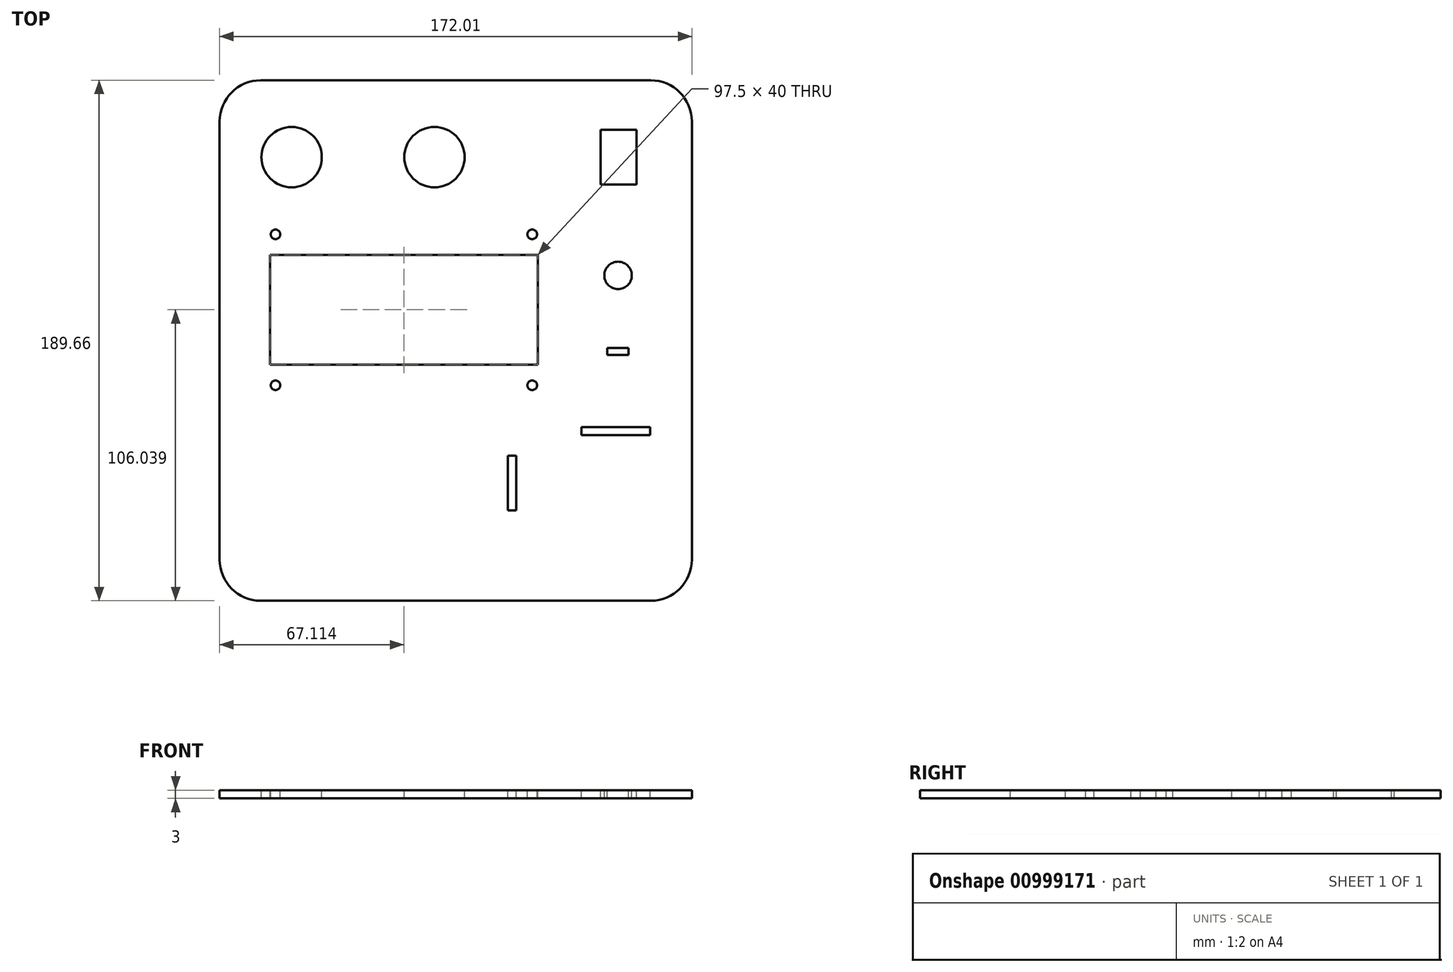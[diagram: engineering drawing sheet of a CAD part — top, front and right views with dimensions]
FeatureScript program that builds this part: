
annotation { "Feature Type Name" : "Feature", "Feature Type Description" : "" }
export const myFeature = defineFeature(function(context is Context, id is Id, definition is map)
    precondition{}
    {
        {
            var Q0;
            Q0=qCreatedBy(makeId("Top.planeOp"),FACE);
            var sketch = newSketch(context, id + "F0", { "sketchPlane" : qUnion([Q0])});
            skPoint(sketch, "E0.middle", {"position": v(0, 0) * mm});
            skLineSegment(sketch, "E1.bottom", {"start": v(124.5, -135.5) * mm, "end": v(-124.5, -135.5) * mm});
            skLineSegment(sketch, "E1.top", {"start": v(124.5, 135.5) * mm, "end": v(-124.5, 135.5) * mm});
            skLineSegment(sketch, "E1.left", {"start": v(124.5, -135.5) * mm, "end": v(124.5, 135.5) * mm});
            skLineSegment(sketch, "E1.right", {"start": v(-124.5, -135.5) * mm, "end": v(-124.5, 135.5) * mm});
            skLineSegment(sketch, "E2.0", {"start": v(113.5, 124.5) * mm, "end": v(-113.5, 124.5) * mm});
            skLineSegment(sketch, "E2.1", {"start": v(113.5, -124.5) * mm, "end": v(113.5, 124.5) * mm});
            skLineSegment(sketch, "E2.2", {"start": v(113.5, -124.5) * mm, "end": v(-113.5, -124.5) * mm});
            skLineSegment(sketch, "E2.3", {"start": v(-113.5, -124.5) * mm, "end": v(-113.5, 124.5) * mm});
            skSolve(sketch);
        }
        {
            var Q0;
            Q0 = qSketchRegion(id + "F0", true);
            var Q1;
            Q1=makeQuery(id+"F0.imprint","IMPRINT",FACE,{"disambiguationData":[TD([[makeQuery(id+"F0.imprint","IMPRINT",EDGE,{"derivedFrom":sQuery(id+"F0.wireOp",EDGE,"E2.0")}),1.0]])]});
            extrude(context, id + "F1", {"entities" : qUnion([Q0, Q1]), "depth" : 3 * mm, "offsetDistance" : 25 * mm});
        }
        {
            var Q0;
            Q0=makeQuery(id+"F1.opExtrude","CAP_FACE",FACE,{"disambiguationData":[OSD([sQuery(id+"F0.wireOp",EDGE,"E1.bottom"),sQuery(id+"F0.wireOp",EDGE,"E1.top"),sQuery(id+"F0.wireOp",EDGE,"E1.left"),sQuery(id+"F0.wireOp",EDGE,"E1.right")])],"isStart":false});
            var sketch = newSketch(context, id + "F2", { "sketchPlane" : qUnion([Q0])});
            skLineSegment(sketch, "E3.bottom", {"start": v(54.76, 20.35) * mm, "end": v(-42.74, 20.35) * mm});
            skLineSegment(sketch, "E3.top", {"start": v(54.76, 60.35) * mm, "end": v(-42.74, 60.35) * mm});
            skLineSegment(sketch, "E3.left", {"start": v(54.76, 20.35) * mm, "end": v(54.76, 60.35) * mm});
            skLineSegment(sketch, "E3.right", {"start": v(-42.74, 20.35) * mm, "end": v(-42.74, 60.35) * mm});
            skPoint(sketch, "E3.middle", {"position": v(6.01, 40.35) * mm});
            skLineSegment(sketch, "E4.bottom", {"start": v(44.01, -42.25) * mm, "end": v(-31.99, -42.25) * mm, "construction": true});
            skLineSegment(sketch, "E4.top", {"start": v(44.01, -3.25) * mm, "end": v(-31.99, -3.25) * mm, "construction": true});
            skLineSegment(sketch, "E4.left", {"start": v(54.01, -32.25) * mm, "end": v(54.01, -13.25) * mm, "construction": true});
            skLineSegment(sketch, "E4.right", {"start": v(-41.99, -32.25) * mm, "end": v(-41.99, -13.25) * mm, "construction": true});
            skPoint(sketch, "E4.middle", {"position": v(6.01, -22.75) * mm});
            skPoint(sketch, "E5.visualSharp", {"position": v(-41.99, -3.25) * mm});
            skArc(sketch, "E5.filletArc", {"start": v(-31.99, -3.25) * mm, "mid": v(-39.06, -6.18) * mm, "end": v(-41.99, -13.25) * mm, "construction": true});
            skPoint(sketch, "E6.visualSharp", {"position": v(-41.99, -42.25) * mm});
            skArc(sketch, "E6.filletArc", {"start": v(-41.99, -32.25) * mm, "mid": v(-39.06, -39.32) * mm, "end": v(-31.99, -42.25) * mm, "construction": true});
            skPoint(sketch, "E7.visualSharp", {"position": v(54.01, -42.25) * mm});
            skArc(sketch, "E7.filletArc", {"start": v(44.01, -42.25) * mm, "mid": v(51.09, -39.32) * mm, "end": v(54.01, -32.25) * mm, "construction": true});
            skPoint(sketch, "E8.visualSharp", {"position": v(54.01, -3.25) * mm});
            skArc(sketch, "E8.filletArc", {"start": v(54.01, -13.25) * mm, "mid": v(51.09, -6.18) * mm, "end": v(44.01, -3.25) * mm, "construction": true});
            skCircle(sketch, "E9", {"center": v(-34.87, 95.98) * mm, "radius": 11 * mm});
            skCircle(sketch, "E10", {"center": v(17.17, 95.98) * mm, "radius": 11 * mm});
            skLineSegment(sketch, "E11.bottom", {"start": v(52.76, 12.85) * mm, "end": v(-40.74, 12.85) * mm, "construction": true});
            skLineSegment(sketch, "E11.top", {"start": v(52.76, 67.85) * mm, "end": v(-40.74, 67.85) * mm, "construction": true});
            skLineSegment(sketch, "E11.left", {"start": v(52.76, 12.85) * mm, "end": v(52.76, 67.85) * mm, "construction": true});
            skLineSegment(sketch, "E11.right", {"start": v(-40.74, 12.85) * mm, "end": v(-40.74, 67.85) * mm, "construction": true});
            skCircle(sketch, "E12", {"center": v(-40.74, 67.85) * mm, "radius": 1.75 * mm});
            skCircle(sketch, "E13", {"center": v(52.76, 67.85) * mm, "radius": 1.75 * mm});
            skCircle(sketch, "E14", {"center": v(52.76, 12.85) * mm, "radius": 1.75 * mm});
            skCircle(sketch, "E15", {"center": v(-40.74, 12.85) * mm, "radius": 1.75 * mm});
            skLineSegment(sketch, "E16", {"start": v(6.01, 40.35) * mm, "end": v(6.01, -22.75) * mm, "construction": true});
            skLineSegment(sketch, "E17.bottom", {"start": v(43.95, -32.75) * mm, "end": v(46.95, -32.75) * mm});
            skLineSegment(sketch, "E17.top", {"start": v(43.95, -12.75) * mm, "end": v(46.95, -12.75) * mm});
            skLineSegment(sketch, "E17.left", {"start": v(43.95, -32.75) * mm, "end": v(43.95, -12.75) * mm});
            skLineSegment(sketch, "E17.right", {"start": v(46.95, -32.75) * mm, "end": v(46.95, -12.75) * mm});
            skPoint(sketch, "E17.middle", {"position": v(45.45, -22.75) * mm});
            skPoint(sketch, "E17.middle.positionSnap0", {"position": v(54.01, -22.75) * mm});
            skPoint(sketch, "E17.centerSnap0", {"position": v(54.01, -22.75) * mm});
            skLineSegment(sketch, "E18.bottom", {"start": v(90.7, 85.98) * mm, "end": v(77.7, 85.98) * mm});
            skLineSegment(sketch, "E18.top", {"start": v(90.7, 105.98) * mm, "end": v(77.7, 105.98) * mm});
            skLineSegment(sketch, "E18.left", {"start": v(90.7, 85.98) * mm, "end": v(90.7, 105.98) * mm});
            skLineSegment(sketch, "E18.right", {"start": v(77.7, 85.98) * mm, "end": v(77.7, 105.98) * mm});
            skPoint(sketch, "E18.middle", {"position": v(84.2, 95.98) * mm});
            skLineSegment(sketch, "E19.bottom", {"start": v(70.65, -2.33) * mm, "end": v(95.65, -2.33) * mm});
            skLineSegment(sketch, "E19.top", {"start": v(70.65, -5.33) * mm, "end": v(95.65, -5.33) * mm});
            skLineSegment(sketch, "E19.left", {"start": v(70.65, -2.33) * mm, "end": v(70.65, -5.33) * mm});
            skLineSegment(sketch, "E19.right", {"start": v(95.65, -2.33) * mm, "end": v(95.65, -5.33) * mm});
            skLineSegment(sketch, "E20.bottom", {"start": v(65.56, -5.33) * mm, "end": v(100.56, -5.33) * mm, "construction": true});
            skLineSegment(sketch, "E20.top", {"start": v(65.56, -56.33) * mm, "end": v(100.56, -56.33) * mm, "construction": true});
            skLineSegment(sketch, "E20.left", {"start": v(65.56, -5.33) * mm, "end": v(65.56, -56.33) * mm, "construction": true});
            skLineSegment(sketch, "E20.right", {"start": v(100.56, -5.33) * mm, "end": v(100.56, -56.33) * mm, "construction": true});
            skCircle(sketch, "E21", {"center": v(84.01, 52.88) * mm, "radius": 5 * mm});
            skLineSegment(sketch, "E22.bottom", {"start": v(80.15, 26.44) * mm, "end": v(87.85, 26.44) * mm});
            skLineSegment(sketch, "E22.top", {"start": v(80.15, 23.94) * mm, "end": v(87.85, 23.94) * mm});
            skLineSegment(sketch, "E22.left", {"start": v(80.15, 26.44) * mm, "end": v(80.15, 23.94) * mm});
            skLineSegment(sketch, "E22.right", {"start": v(87.85, 26.44) * mm, "end": v(87.85, 23.94) * mm});
            skSolve(sketch);
        }
        {
            var Q0;
            Q0 = qSketchRegion(id + "F2", true);
            extrude(context, id + "F3", {"entities" : qUnion([Q0]), "operationType" : NewBodyOperationType.REMOVE, "oppositeDirection" : true, "depth" : 25 * mm, "offsetDistance" : 25 * mm});
        }
        {
            var Q0;
            Q0=makeQuery(id+"F1.opExtrude","CAP_FACE",FACE,{"disambiguationData":[OSD([sQuery(id+"F0.wireOp",EDGE,"E1.bottom"),sQuery(id+"F0.wireOp",EDGE,"E1.top"),sQuery(id+"F0.wireOp",EDGE,"E1.left"),sQuery(id+"F0.wireOp",EDGE,"E1.right")])],"isStart":false});
            var sketch = newSketch(context, id + "F4", { "sketchPlane" : qUnion([Q0])});
            skLineSegment(sketch, "E23.bottom", {"start": v(-46.1, 123.97) * mm, "end": v(95.9, 123.97) * mm});
            skLineSegment(sketch, "E23.top", {"start": v(-46.1, -65.69) * mm, "end": v(95.9, -65.69) * mm});
            skLineSegment(sketch, "E23.left", {"start": v(-61.1, 108.97) * mm, "end": v(-61.1, -50.69) * mm});
            skLineSegment(sketch, "E23.right", {"start": v(110.9, 108.97) * mm, "end": v(110.9, -50.69) * mm});
            skPoint(sketch, "E24.visualSharp", {"position": v(-61.1, 123.97) * mm});
            skArc(sketch, "E24.filletArc", {"start": v(-46.1, 123.97) * mm, "mid": v(-56.7, 119.58) * mm, "end": v(-61.1, 108.97) * mm});
            skPoint(sketch, "E25.visualSharp", {"position": v(-61.1, -65.69) * mm});
            skArc(sketch, "E25.filletArc", {"start": v(-61.1, -50.69) * mm, "mid": v(-56.7, -61.3) * mm, "end": v(-46.1, -65.69) * mm});
            skPoint(sketch, "E26.visualSharp", {"position": v(110.9, -65.69) * mm});
            skArc(sketch, "E26.filletArc", {"start": v(95.9, -65.69) * mm, "mid": v(106.51, -61.3) * mm, "end": v(110.9, -50.69) * mm});
            skPoint(sketch, "E27.visualSharp", {"position": v(110.9, 123.97) * mm});
            skArc(sketch, "E27.filletArc", {"start": v(110.9, 108.97) * mm, "mid": v(106.51, 119.58) * mm, "end": v(95.9, 123.97) * mm});
            skSolve(sketch);
        }
        {
            var Q0;
            Q0=makeQuery(id+"F4.imprint","IMPRINT",FACE,{"disambiguationData":[TD([[makeQuery(id+"F4.imprint","IMPRINT",EDGE,{"derivedFrom":sQuery(id+"F4.wireOp",EDGE,"E23.bottom")}),1.0]])]});
            extrude(context, id + "F5", {"entities" : qUnion([Q0]), "operationType" : NewBodyOperationType.REMOVE, "endBound" : BoundingType.UP_TO_NEXT, "oppositeDirection" : true, "depth" : 25 * mm, "offsetDistance" : 25 * mm});
        }
    });
